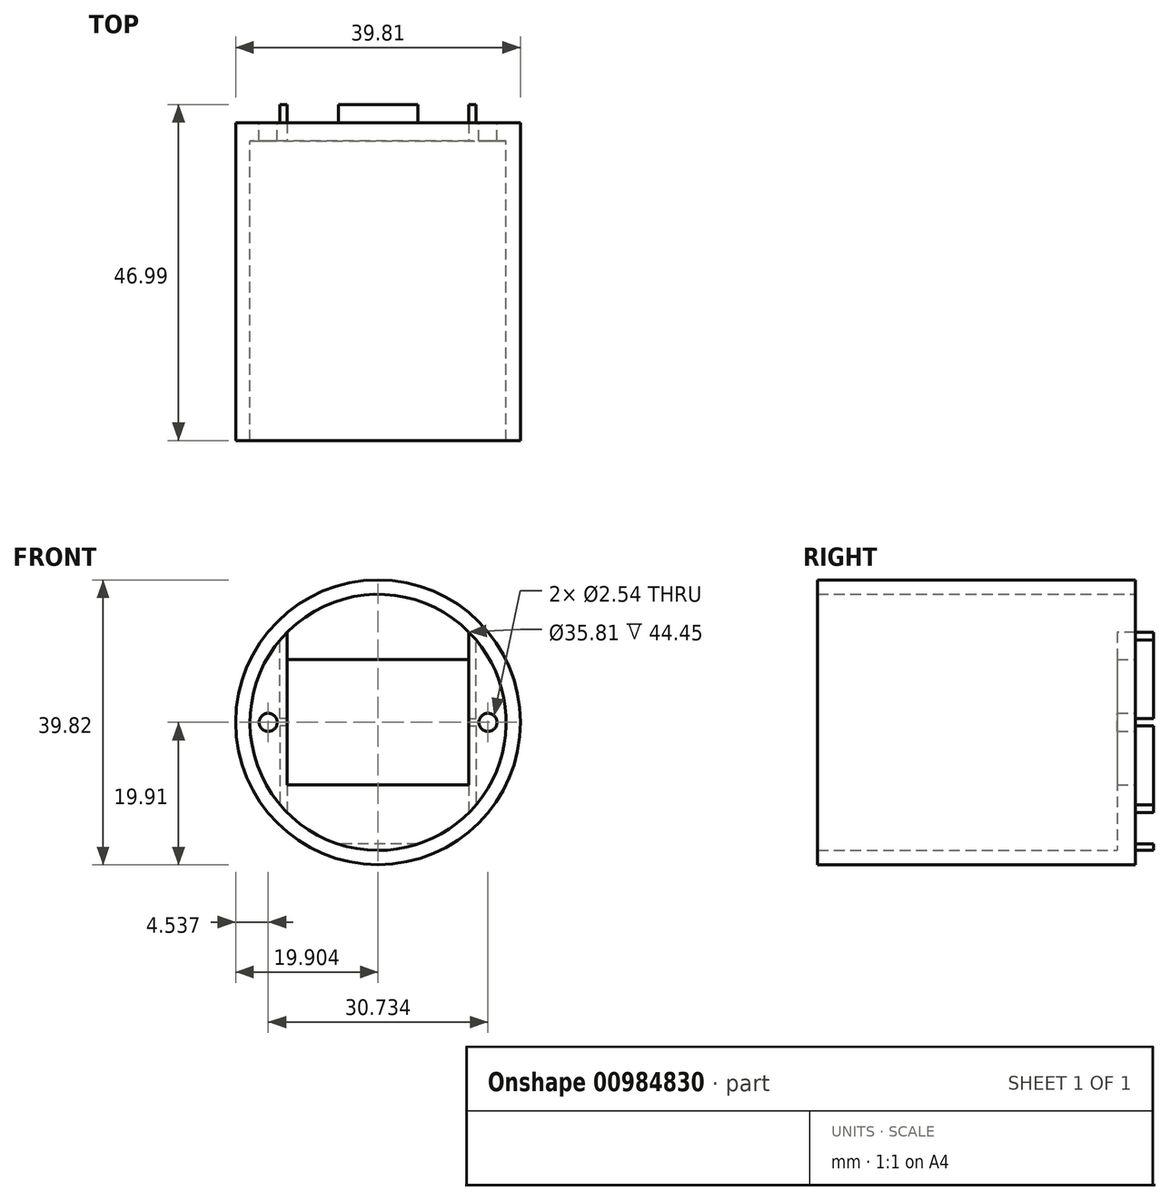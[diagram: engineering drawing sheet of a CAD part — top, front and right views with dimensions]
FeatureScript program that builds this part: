
annotation { "Feature Type Name" : "Feature", "Feature Type Description" : "" }
export const myFeature = defineFeature(function(context is Context, id is Id, definition is map)
    precondition{}
    {
        {
            var Q0;
            Q0=qCreatedBy(makeId("Front.planeOp"),FACE);
            cPlane(context, id + "F0", {"entities" : qUnion([Q0]), "cplaneType" : CPlaneType.OFFSET, "offset" : 25.4 * mm, "width" : 152.4 * mm, "height" : 152.4 * mm});
        }
        {
            var Q0;
            Q0=qCreatedBy(id+"F0.planeOp",FACE);
            var sketch = newSketch(context, id + "F1", { "sketchPlane" : qUnion([Q0])});
            skLineSegment(sketch, "E0", {"start": v(0, 0) * mm, "end": v(5, 0) * mm});
            skCircle(sketch, "E1", {"center": v(5, 0) * mm, "radius": 17.9 * mm});
            skCircle(sketch, "E2.0", {"center": v(5, 0) * mm, "radius": 19.9 * mm});
            skSolve(sketch);
        }
        {
            var Q0;
            Q0=makeQuery(id+"F1.imprint","IMPRINT",FACE,{"disambiguationData":[TD([[makeQuery(id+"F1.imprint","IMPRINT",EDGE,{"derivedFrom":sQuery(id+"F1.wireOp",EDGE,"E1")}),-1.0]])]});
            extrude(context, id + "F2", {"entities" : qUnion([Q0]), "endBound" : BoundingType.SYMMETRIC, "depth" : 38.1 * mm, "offsetDistance" : 25.4 * mm});
        }
        {
            var Q0;
            Q0=qCreatedBy(makeId("Front.planeOp"),FACE);
            var sketch = newSketch(context, id + "F3", { "sketchPlane" : qUnion([Q0])});
            skCircle(sketch, "E3", {"center": v(5, 0) * mm, "radius": 17.9 * mm});
            skLineSegment(sketch, "E4", {"start": v(17.7, 0) * mm, "end": v(22.91, 0) * mm});
            skLineSegment(sketch, "E5", {"start": v(22.91, 0) * mm, "end": v(17.7, 0) * mm});
            skLineSegment(sketch, "E6", {"start": v(-12.9, 0) * mm, "end": v(-10.36, 0) * mm});
            skLineSegment(sketch, "E7", {"start": v(22.91, 0) * mm, "end": v(20.37, 0) * mm});
            skCircle(sketch, "E8", {"center": v(20.37, 0) * mm, "radius": 1.27 * mm});
            skCircle(sketch, "E9", {"center": v(-10.36, 0) * mm, "radius": 1.27 * mm});
            skLineSegment(sketch, "E10", {"start": v(5, 0) * mm, "end": v(5, 17.9) * mm});
            skLineSegment(sketch, "E11", {"start": v(5, 17.9) * mm, "end": v(5, -17.9) * mm});
            skLineSegment(sketch, "E12.bottom", {"start": v(0, 0.5) * mm, "end": v(10, 0.5) * mm});
            skLineSegment(sketch, "E12.top", {"start": v(0, -0.5) * mm, "end": v(10, -0.5) * mm});
            skLineSegment(sketch, "E13", {"start": v(5, -0.5) * mm, "end": v(5, -17.02) * mm});
            skLineSegment(sketch, "E14", {"start": v(5, 0.5) * mm, "end": v(5, 17.02) * mm});
            skLineSegment(sketch, "E15", {"start": v(5, -8.76) * mm, "end": v(-7.7, -8.76) * mm});
            skLineSegment(sketch, "E16", {"start": v(5, -8.76) * mm, "end": v(17.7, -8.76) * mm});
            skLineSegment(sketch, "E17", {"start": v(5, -17.02) * mm, "end": v(-7.7, -17.02) * mm});
            skLineSegment(sketch, "E18", {"start": v(10, -0.5) * mm, "end": v(17.7, -0.5) * mm});
            skLineSegment(sketch, "E19.bottom", {"start": v(17.7, -0.5) * mm, "end": v(-7.7, -0.5) * mm});
            skLineSegment(sketch, "E19.top", {"start": v(17.7, -17.02) * mm, "end": v(-7.7, -17.02) * mm});
            skLineSegment(sketch, "E19.left", {"start": v(17.7, -0.5) * mm, "end": v(17.7, -17.02) * mm});
            skLineSegment(sketch, "E19.right", {"start": v(-7.7, -0.5) * mm, "end": v(-7.7, -17.02) * mm});
            skLineSegment(sketch, "E20", {"start": v(-7.7, -0.5) * mm, "end": v(-8.71, -0.5) * mm});
            skLineSegment(sketch, "E21", {"start": v(-8.71, -0.5) * mm, "end": v(-8.71, -11.51) * mm});
            skLineSegment(sketch, "E22", {"start": v(17.7, -0.5) * mm, "end": v(18.72, -0.5) * mm});
            skLineSegment(sketch, "E23", {"start": v(18.72, -0.5) * mm, "end": v(18.72, -11.51) * mm});
            skLineSegment(sketch, "E24.bottom", {"start": v(-7.7, -0.5) * mm, "end": v(17.7, -0.5) * mm});
            skLineSegment(sketch, "E24.top", {"start": v(-7.7, 0.5) * mm, "end": v(17.7, 0.5) * mm});
            skLineSegment(sketch, "E24.left", {"start": v(-7.7, -0.5) * mm, "end": v(-7.7, 0.5) * mm});
            skLineSegment(sketch, "E24.right", {"start": v(17.7, -0.5) * mm, "end": v(17.7, 0.5) * mm});
            skLineSegment(sketch, "E25", {"start": v(5, 17.02) * mm, "end": v(-0.57, 17.02) * mm});
            skLineSegment(sketch, "E26", {"start": v(-0.57, 17.02) * mm, "end": v(10.58, 17.02) * mm});
            skLineSegment(sketch, "E27", {"start": v(5, 0.5) * mm, "end": v(5, 8.76) * mm});
            skLineSegment(sketch, "E28", {"start": v(5, 8.76) * mm, "end": v(-7.7, 8.76) * mm});
            skLineSegment(sketch, "E29", {"start": v(5, 8.76) * mm, "end": v(17.7, 8.76) * mm});
            skLineSegment(sketch, "E30", {"start": v(17.7, 8.76) * mm, "end": v(17.7, 12.62) * mm});
            skLineSegment(sketch, "E31", {"start": v(18.72, 8.76) * mm, "end": v(18.72, 11.51) * mm});
            skLineSegment(sketch, "E32", {"start": v(17.7, 0.5) * mm, "end": v(18.72, 0.5) * mm});
            skLineSegment(sketch, "E33.left", {"start": v(17.7, 0.5) * mm, "end": v(17.7, 8.76) * mm});
            skLineSegment(sketch, "E33.right", {"start": v(18.72, 0.5) * mm, "end": v(18.72, 8.76) * mm});
            skLineSegment(sketch, "E34", {"start": v(-7.7, 8.76) * mm, "end": v(-7.7, 0.5) * mm});
            skLineSegment(sketch, "E35", {"start": v(-7.7, 8.76) * mm, "end": v(-7.7, 12.62) * mm});
            skLineSegment(sketch, "E36", {"start": v(-7.7, 0.5) * mm, "end": v(-8.71, 0.5) * mm});
            skLineSegment(sketch, "E37", {"start": v(-8.71, 0.5) * mm, "end": v(-8.71, 11.51) * mm});
            skLineSegment(sketch, "E38.trimOffspring", {"start": v(-7.7, 0) * mm, "end": v(-12.9, 0) * mm});
            skSolve(sketch);
        }
        {
            var Q0;
            {var subQ0=sQuery(id+"F3.wireOp",EDGE,"E11");var subQ1=sQuery(id+"F3.wireOp",EDGE,"E3");var subQ2=makeQuery(id+"F3.imprint","INTERSECT",VERTEX,{"disambiguationData":[OD(1.0)],"derivedFrom":[subQ1,subQ0]});Q0=makeQuery(id+"F3.imprint","IMPRINT",FACE,{"disambiguationData":[TD([[makeQuery(id+"F3.imprint","IMPRINT",EDGE,{"disambiguationData":[TD([[subQ2,1.0]])],"derivedFrom":subQ1}),1.0]])]});}
            var Q1;
            {var subQ0=sQuery(id+"F3.wireOp",EDGE,"E11");var subQ1=sQuery(id+"F3.wireOp",EDGE,"E3");var subQ2=makeQuery(id+"F3.imprint","INTERSECT",VERTEX,{"disambiguationData":[OD(1.0)],"derivedFrom":[subQ1,subQ0]});Q1=makeQuery(id+"F3.imprint","IMPRINT",FACE,{"disambiguationData":[TD([[makeQuery(id+"F3.imprint","IMPRINT",EDGE,{"disambiguationData":[TD([[subQ2,-1.0]])],"derivedFrom":subQ1}),1.0]])]});}
            var Q2;
            {var subQ0=sQuery(id+"F3.wireOp",EDGE,"E20");Q2=makeQuery(id+"F3.imprint","IMPRINT",FACE,{"disambiguationData":[TD([[makeQuery(id+"F3.imprint","IMPRINT",EDGE,{"derivedFrom":subQ0}),1.0]])]});}
            var Q3;
            Q3=makeQuery(id+"F3.imprint","IMPRINT",FACE,{"disambiguationData":[TD([[makeQuery(id+"F3.imprint","IMPRINT",EDGE,{"derivedFrom":sQuery(id+"F3.wireOp",EDGE,"E34")}),-1.0]])]});
            var Q4;
            {var subQ1=sQuery(id+"F3.wireOp",EDGE,"E11");var subQ4=makeQuery(id+"F3.imprint","IMPRINT",VERTEX,{"derivedFrom":subQ1});Q4=makeQuery(id+"F3.imprint","IMPRINT",FACE,{"disambiguationData":[TD([[makeQuery(id+"F3.imprint","IMPRINT",EDGE,{"disambiguationData":[TD([[subQ4,1.0]])],"derivedFrom":subQ1}),-1.0]])]});}
            var Q5;
            {var subQ1=sQuery(id+"F3.wireOp",EDGE,"E11");var subQ8=makeQuery(id+"F3.imprint","IMPRINT",VERTEX,{"derivedFrom":subQ1});Q5=makeQuery(id+"F3.imprint","IMPRINT",FACE,{"disambiguationData":[TD([[makeQuery(id+"F3.imprint","IMPRINT",EDGE,{"disambiguationData":[TD([[subQ8,1.0]])],"derivedFrom":subQ1}),1.0]])]});}
            var Q6;
            {var subQ0=sQuery(id+"F3.wireOp",EDGE,"E22");Q6=makeQuery(id+"F3.imprint","IMPRINT",FACE,{"disambiguationData":[TD([[makeQuery(id+"F3.imprint","IMPRINT",EDGE,{"derivedFrom":subQ0}),-1.0]])]});}
            var Q7;
            {var subQ1=sQuery(id+"F3.wireOp",EDGE,"E30");Q7=makeQuery(id+"F3.imprint","IMPRINT",FACE,{"disambiguationData":[TD([[makeQuery(id+"F3.imprint","IMPRINT",EDGE,{"derivedFrom":subQ1}),-1.0]])]});}
            var Q8;
            {var subQ0=sQuery(id+"F3.wireOp",EDGE,"E11");var subQ1=sQuery(id+"F3.wireOp",EDGE,"E3");var subQ2=makeQuery(id+"F3.imprint","INTERSECT",VERTEX,{"disambiguationData":[OD(0.0)],"derivedFrom":[subQ1,subQ0]});Q8=makeQuery(id+"F3.imprint","IMPRINT",FACE,{"disambiguationData":[TD([[makeQuery(id+"F3.imprint","IMPRINT",EDGE,{"disambiguationData":[TD([[subQ2,1.0]])],"derivedFrom":subQ1}),1.0]])]});}
            var Q9;
            {var subQ0=sQuery(id+"F3.wireOp",EDGE,"E11");var subQ1=sQuery(id+"F3.wireOp",EDGE,"E3");var subQ2=makeQuery(id+"F3.imprint","INTERSECT",VERTEX,{"disambiguationData":[OD(0.0)],"derivedFrom":[subQ1,subQ0]});Q9=makeQuery(id+"F3.imprint","IMPRINT",FACE,{"disambiguationData":[TD([[makeQuery(id+"F3.imprint","IMPRINT",EDGE,{"disambiguationData":[TD([[subQ2,-1.0]])],"derivedFrom":subQ1}),1.0]])]});}
            extrude(context, id + "F4", {"entities" : qUnion([Q0, Q1, Q2, Q3, Q4, Q5, Q6, Q7, Q8, Q9]), "endBound" : BoundingType.SYMMETRIC, "oppositeDirection" : true, "depth" : 5.08 * mm, "offsetDistance" : 25.4 * mm});
        }
        {
            var Q0;
            Q0=makeQuery(id+"F2.opExtrude","CAP_FACE",FACE,{"disambiguationData":[OSD([sQuery(id+"F1.wireOp",EDGE,"E1"),sQuery(id+"F1.wireOp",EDGE,"E2.0")])],"isStart":true});
            extrude(context, id + "F5", {"entities" : qUnion([Q0]), "operationType" : NewBodyOperationType.ADD, "depth" : 6.35 * mm, "offsetDistance" : 25.4 * mm});
        }
        {
            var Q0;
            {var subQ1=sQuery(id+"F3.wireOp",EDGE,"E14");Q0=makeQuery(id+"F3.imprint","IMPRINT",FACE,{"disambiguationData":[TD([[makeQuery(id+"F3.imprint","IMPRINT",EDGE,{"derivedFrom":subQ1}),-1.0]])]});}
            var Q1;
            {var subQ1=sQuery(id+"F3.wireOp",EDGE,"E14");Q1=makeQuery(id+"F3.imprint","IMPRINT",FACE,{"disambiguationData":[TD([[makeQuery(id+"F3.imprint","IMPRINT",EDGE,{"derivedFrom":subQ1}),1.0]])]});}
            var Q2;
            {var subQ0=sQuery(id+"F3.wireOp",EDGE,"E36");Q2=makeQuery(id+"F3.imprint","IMPRINT",FACE,{"disambiguationData":[TD([[makeQuery(id+"F3.imprint","IMPRINT",EDGE,{"derivedFrom":subQ0}),1.0]])]});}
            var Q3;
            {var subQ1=sQuery(id+"F3.wireOp",EDGE,"E20");Q3=makeQuery(id+"F3.imprint","IMPRINT",FACE,{"disambiguationData":[TD([[makeQuery(id+"F3.imprint","IMPRINT",EDGE,{"derivedFrom":subQ1}),-1.0]])]});}
            var Q4;
            {var subQ0=sQuery(id+"F3.wireOp",EDGE,"E15");Q4=makeQuery(id+"F3.imprint","IMPRINT",FACE,{"disambiguationData":[TD([[makeQuery(id+"F3.imprint","IMPRINT",EDGE,{"derivedFrom":subQ0}),1.0]])]});}
            var Q5;
            {var subQ0=sQuery(id+"F3.wireOp",EDGE,"E16");Q5=makeQuery(id+"F3.imprint","IMPRINT",FACE,{"disambiguationData":[TD([[makeQuery(id+"F3.imprint","IMPRINT",EDGE,{"derivedFrom":subQ0}),-1.0]])]});}
            var Q6;
            {var subQ10=sQuery(id+"F3.wireOp",EDGE,"E22");Q6=makeQuery(id+"F3.imprint","IMPRINT",FACE,{"disambiguationData":[TD([[makeQuery(id+"F3.imprint","IMPRINT",EDGE,{"derivedFrom":subQ10}),1.0]])]});}
            var Q7;
            {var subQ9=sQuery(id+"F3.wireOp",EDGE,"E31");Q7=makeQuery(id+"F3.imprint","IMPRINT",FACE,{"disambiguationData":[TD([[makeQuery(id+"F3.imprint","IMPRINT",EDGE,{"derivedFrom":subQ9}),-1.0]])]});}
            extrude(context, id + "F6", {"entities" : qUnion([Q0, Q1, Q2, Q3, Q4, Q5, Q6, Q7]), "operationType" : NewBodyOperationType.ADD, "depth" : 2.54 * mm, "offsetDistance" : 25.4 * mm});
        }
        {
            var Q0;
            Q0=qCreatedBy(makeId("Front.planeOp"),FACE);
            var sketch = newSketch(context, id + "F7", { "sketchPlane" : qUnion([Q0])});
            skLineSegment(sketch, "E39", {"start": v(0, 0) * mm, "end": v(5, 0) * mm});
            skLineSegment(sketch, "E40.bottom", {"start": v(17.7, 8.76) * mm, "end": v(-7.7, 8.76) * mm});
            skLineSegment(sketch, "E40.top", {"start": v(17.7, -8.76) * mm, "end": v(-7.7, -8.76) * mm});
            skLineSegment(sketch, "E40.left", {"start": v(17.7, 8.76) * mm, "end": v(17.7, -8.76) * mm});
            skLineSegment(sketch, "E40.right", {"start": v(-7.7, 8.76) * mm, "end": v(-7.7, -8.76) * mm});
            skPoint(sketch, "E40.middle", {"position": v(5, 0) * mm});
            skSolve(sketch);
        }
        {
            var Q0;
            Q0 = qSketchRegion(id + "F7", true);
            extrude(context, id + "F8", {"entities" : qUnion([Q0]), "depth" : 2.54 * mm, "offsetDistance" : 25.4 * mm});
        }
    });
